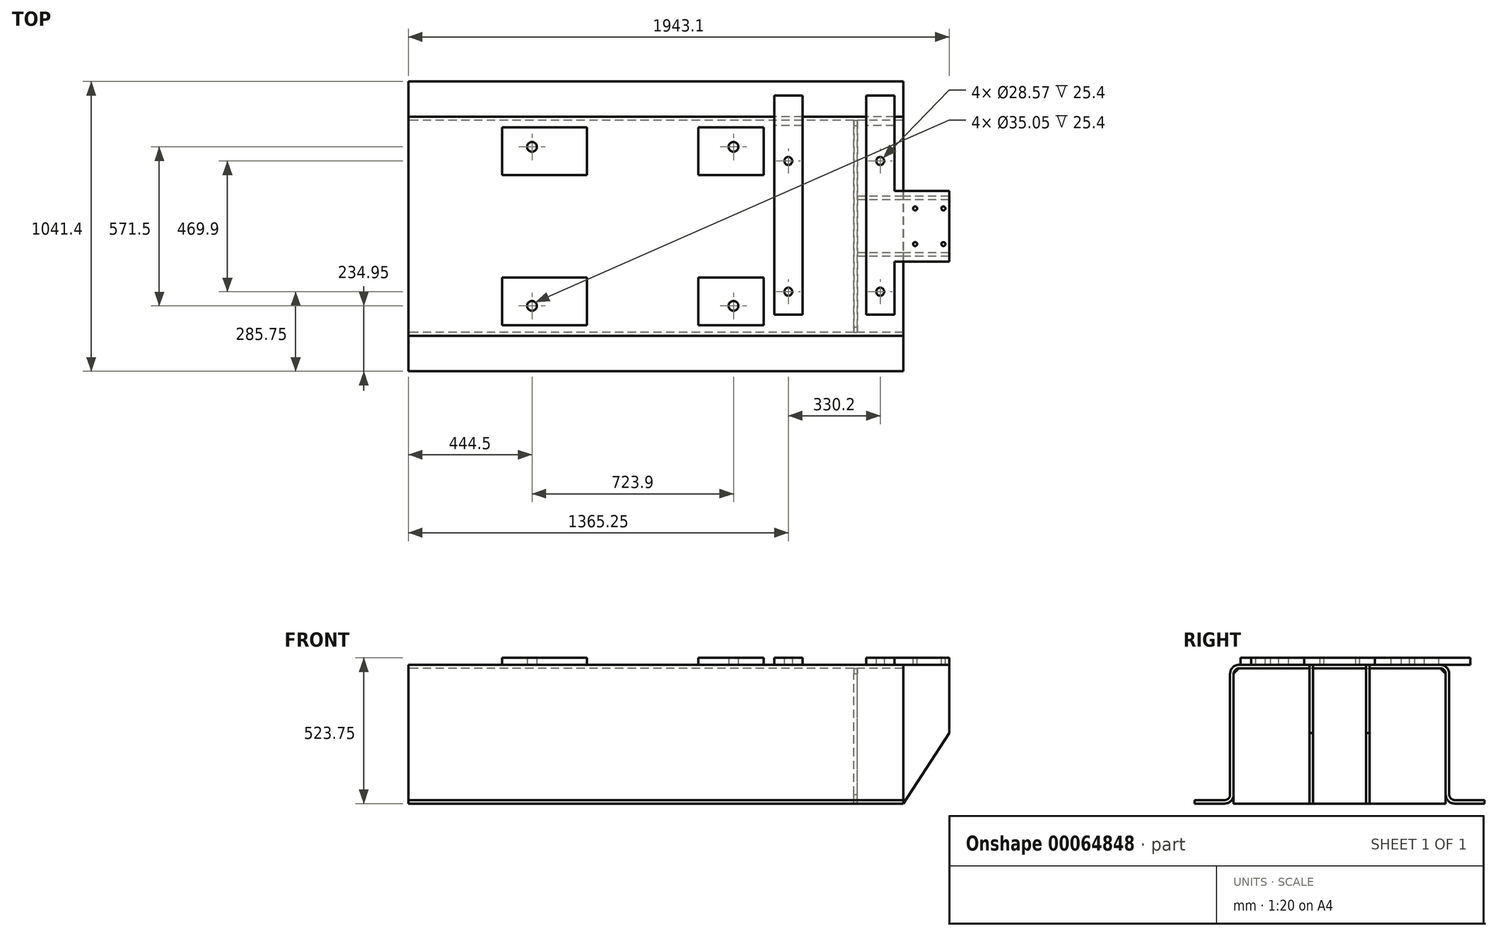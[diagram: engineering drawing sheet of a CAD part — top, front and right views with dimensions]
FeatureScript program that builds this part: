
annotation { "Feature Type Name" : "Feature", "Feature Type Description" : "" }
export const myFeature = defineFeature(function(context is Context, id is Id, definition is map)
    precondition{}
    {
        {
            var Q0;
            Q0=qCreatedBy(makeId("Right.planeOp"),FACE);
            var sketch = newSketch(context, id + "F0", { "sketchPlane" : qUnion([Q0])});
            skLineSegment(sketch, "E0", {"start": v(-520.7, 0) * mm, "end": v(-412.75, 0) * mm});
            skLineSegment(sketch, "E1.0", {"start": v(-520.7, 12.7) * mm, "end": v(-412.75, 12.7) * mm});
            skLineSegment(sketch, "E2", {"start": v(-520.7, 0) * mm, "end": v(-520.7, 12.7) * mm});
            skLineSegment(sketch, "E3", {"start": v(0, 498.35) * mm, "end": v(0, -237.5) * mm, "construction": true});
            skLineSegment(sketch, "E4.0", {"start": v(-381, 31.75) * mm, "end": v(-381, 466.6) * mm});
            skLineSegment(sketch, "E5.0", {"start": v(-393.7, 31.75) * mm, "end": v(-393.7, 466.6) * mm});
            skLineSegment(sketch, "E6.0", {"start": v(-361.95, 498.35) * mm, "end": v(0, 498.35) * mm});
            skLineSegment(sketch, "E7.0", {"start": v(-361.95, 485.65) * mm, "end": v(0, 485.65) * mm});
            skPoint(sketch, "E8.orphan", {"position": v(-520.7, 181.66) * mm});
            skPoint(sketch, "E9.visualSharp", {"position": v(-381, 485.65) * mm});
            skArc(sketch, "E9.filletArc", {"start": v(-361.95, 485.65) * mm, "mid": v(-375.42, 480.07) * mm, "end": v(-381, 466.6) * mm});
            skPoint(sketch, "E10.visualSharp", {"position": v(-393.7, 12.7) * mm});
            skArc(sketch, "E10.filletArc", {"start": v(-412.75, 12.7) * mm, "mid": v(-399.28, 18.28) * mm, "end": v(-393.7, 31.75) * mm});
            skPoint(sketch, "E11.visualSharp", {"position": v(-393.7, 498.35) * mm});
            skArc(sketch, "E11.filletArc", {"start": v(-361.95, 498.35) * mm, "mid": v(-384.4, 489.05) * mm, "end": v(-393.7, 466.6) * mm});
            skPoint(sketch, "E12.visualSharp", {"position": v(-381, 0) * mm});
            skArc(sketch, "E12.filletArc", {"start": v(-412.75, 0) * mm, "mid": v(-390.3, 9.3) * mm, "end": v(-381, 31.75) * mm});
            skLineSegment(sketch, "E13.MirrorCS", {"start": v(520.7, 0) * mm, "end": v(520.7, 12.7) * mm});
            skArc(sketch, "E14.MirrorCS", {"start": v(412.75, 12.7) * mm, "mid": v(399.28, 18.28) * mm, "end": v(393.7, 31.75) * mm});
            skArc(sketch, "E15.MirrorCS", {"start": v(412.75, 0) * mm, "mid": v(390.3, 9.3) * mm, "end": v(381, 31.75) * mm});
            skPoint(sketch, "E16.MirrorP", {"position": v(393.7, 12.7) * mm});
            skPoint(sketch, "E17.MirrorP", {"position": v(381, 0) * mm});
            skLineSegment(sketch, "E18.MirrorCS", {"start": v(520.7, 0) * mm, "end": v(412.75, 0) * mm});
            skLineSegment(sketch, "E19.MirrorCS", {"start": v(520.7, 12.7) * mm, "end": v(412.75, 12.7) * mm});
            skLineSegment(sketch, "E20.MirrorCS", {"start": v(393.7, 31.75) * mm, "end": v(393.7, 466.6) * mm});
            skLineSegment(sketch, "E21.MirrorCS", {"start": v(381, 31.75) * mm, "end": v(381, 466.6) * mm});
            skArc(sketch, "E22.MirrorCS", {"start": v(361.95, 485.65) * mm, "mid": v(375.42, 480.07) * mm, "end": v(381, 466.6) * mm});
            skArc(sketch, "E23.MirrorCS", {"start": v(361.95, 498.35) * mm, "mid": v(384.4, 489.05) * mm, "end": v(393.7, 466.6) * mm});
            skPoint(sketch, "E24.MirrorP", {"position": v(381, 485.65) * mm});
            skPoint(sketch, "E25.MirrorP", {"position": v(393.7, 498.35) * mm});
            skLineSegment(sketch, "E26.MirrorCS", {"start": v(361.95, 485.65) * mm, "end": v(0, 485.65) * mm});
            skLineSegment(sketch, "E27.MirrorCS", {"start": v(361.95, 498.35) * mm, "end": v(0, 498.35) * mm});
            skSolve(sketch);
        }
        {
            var Q0;
            Q0=qSketchRegion(id+"F0",true);
            extrude(context, id + "F1", {"entities" : qUnion([Q0]), "endBound" : BoundingType.SYMMETRIC, "depth" : 1778 * mm});
        }
        {
            var Q0;
            Q0=makeQuery(id+"F1.opExtrude","SWEPT_FACE",FACE,{"disambiguationData":[OSD([sQuery(id+"F0.wireOp",EDGE,"E6.0"),sQuery(id+"F0.wireOp",EDGE,"E27.MirrorCS")])]});
            var sketch = newSketch(context, id + "F2", { "sketchPlane" : qUnion([Q0])});
            skLineSegment(sketch, "E28.0", {"start": v(641.35, 361.95) * mm, "end": v(641.35, -361.95) * mm, "construction": true});
            skLineSegment(sketch, "E29.0", {"start": v(-82.55, 361.95) * mm, "end": v(-82.55, -361.95) * mm, "construction": true});
            skLineSegment(sketch, "E30", {"start": v(-872.47, 0) * mm, "end": v(1054.1, 0) * mm, "construction": true});
            skLineSegment(sketch, "E31.0", {"start": v(476.25, 361.95) * mm, "end": v(476.25, -361.95) * mm, "construction": true});
            skLineSegment(sketch, "E32.0", {"start": v(806.45, 361.95) * mm, "end": v(806.45, -361.95) * mm, "construction": true});
            skLineSegment(sketch, "E33.0", {"start": v(425.45, 469.9) * mm, "end": v(425.45, -317.5) * mm});
            skLineSegment(sketch, "E34.0", {"start": v(527.05, 469.9) * mm, "end": v(527.05, -317.5) * mm});
            skLineSegment(sketch, "E35.0", {"start": v(755.65, 469.9) * mm, "end": v(755.65, -317.5) * mm});
            skLineSegment(sketch, "E36.0", {"start": v(1054.1, 127) * mm, "end": v(1054.1, -127) * mm});
            skLineSegment(sketch, "E37.0", {"start": v(425.45, 469.9) * mm, "end": v(527.05, 469.9) * mm});
            skLineSegment(sketch, "E38.0", {"start": v(755.65, -317.5) * mm, "end": v(857.25, -317.5) * mm});
            skLineSegment(sketch, "E39.trimOffspring", {"start": v(755.65, 469.9) * mm, "end": v(857.25, 469.9) * mm});
            skLineSegment(sketch, "E40.trimOffspring", {"start": v(527.05, -317.5) * mm, "end": v(425.45, -317.5) * mm});
            skLineSegment(sketch, "E41.0", {"start": v(857.25, 469.9) * mm, "end": v(857.25, 127) * mm});
            skLineSegment(sketch, "E42.trimOffspring", {"start": v(857.25, -127) * mm, "end": v(1054.1, -127) * mm});
            skLineSegment(sketch, "E43.trimOffspring", {"start": v(857.25, 127) * mm, "end": v(1054.1, 127) * mm});
            skLineSegment(sketch, "E44.trimOffspring", {"start": v(857.25, -127) * mm, "end": v(857.25, -317.5) * mm});
            skLineSegment(sketch, "E45.0", {"start": v(-872.47, 234.95) * mm, "end": v(1054.1, 234.95) * mm, "construction": true});
            skCircle(sketch, "E46", {"center": v(476.25, 234.95) * mm, "radius": 14.29 * mm});
            skCircle(sketch, "E47", {"center": v(806.45, 234.95) * mm, "radius": 14.29 * mm});
            skCircle(sketch, "E48.MirrorC", {"center": v(806.45, -234.95) * mm, "radius": 14.29 * mm});
            skCircle(sketch, "E49.MirrorC", {"center": v(476.25, -234.95) * mm, "radius": 14.29 * mm});
            skSolve(sketch);
        }
        {
            var Q0;
            Q0=qSketchRegion(id+"F2",true);
            extrude(context, id + "F3", {"entities" : qUnion([Q0]), "operationType" : NewBodyOperationType.ADD, "depth" : 25.4 * mm});
        }
        {
            var Q0;
            Q0=makeQuery(id+"F3.opExtrude","CAP_FACE",FACE,{"disambiguationData":[OSD([sQuery(id+"F2.wireOp",EDGE,"E35.0"),sQuery(id+"F2.wireOp",EDGE,"E36.0"),sQuery(id+"F2.wireOp",EDGE,"E38.0"),sQuery(id+"F2.wireOp",EDGE,"E39.trimOffspring"),sQuery(id+"F2.wireOp",EDGE,"E41.0"),sQuery(id+"F2.wireOp",EDGE,"E42.trimOffspring"),sQuery(id+"F2.wireOp",EDGE,"E43.trimOffspring"),sQuery(id+"F2.wireOp",EDGE,"E44.trimOffspring"),sQuery(id+"F2.wireOp",EDGE,"E47"),sQuery(id+"F2.wireOp",EDGE,"E48.MirrorC")])],"isStart":false});
            var sketch = newSketch(context, id + "F4", { "sketchPlane" : qUnion([Q0])});
            skLineSegment(sketch, "E50", {"start": v(806.45, 234.95) * mm, "end": v(806.45, -249.24) * mm, "construction": true});
            skLineSegment(sketch, "E51", {"start": v(0, 0) * mm, "end": v(1216.03, 0) * mm, "construction": true});
            skPoint(sketch, "E51.endSnap0", {"position": v(1054.1, 0) * mm});
            skLineSegment(sketch, "E52.0", {"start": v(931.93, 234.95) * mm, "end": v(931.93, -249.24) * mm, "construction": true});
            skLineSegment(sketch, "E53.0", {"start": v(1033.53, 234.95) * mm, "end": v(1033.53, -249.24) * mm, "construction": true});
            skLineSegment(sketch, "E54.0", {"start": v(0, 64.52) * mm, "end": v(1216.03, 64.52) * mm, "construction": true});
            skLineSegment(sketch, "E55.0", {"start": v(0, -63.5) * mm, "end": v(1216.03, -63.5) * mm, "construction": true});
            skCircle(sketch, "E56", {"center": v(931.93, 64.52) * mm, "radius": 7.14 * mm});
            skCircle(sketch, "E57", {"center": v(1033.53, 64.52) * mm, "radius": 7.14 * mm});
            skCircle(sketch, "E58", {"center": v(1033.53, -63.5) * mm, "radius": 7.14 * mm});
            skCircle(sketch, "E59", {"center": v(931.93, -63.5) * mm, "radius": 7.14 * mm});
            skSolve(sketch);
        }
        {
            var Q0;
            Q0=qSketchRegion(id+"F4",true);
            extrude(context, id + "F5", {"entities" : qUnion([Q0]), "operationType" : NewBodyOperationType.REMOVE, "endBound" : BoundingType.THROUGH_ALL, "oppositeDirection" : true, "depth" : 25.4 * mm});
        }
        {
            var Q0;
            Q0=makeQuery(id+"F1.opExtrude","CAP_FACE",FACE,{"disambiguationData":[OSD([sQuery(id+"F0.wireOp",EDGE,"E0"),sQuery(id+"F0.wireOp",EDGE,"E1.0"),sQuery(id+"F0.wireOp",EDGE,"E2"),sQuery(id+"F0.wireOp",EDGE,"E4.0"),sQuery(id+"F0.wireOp",EDGE,"E5.0"),sQuery(id+"F0.wireOp",EDGE,"E6.0"),sQuery(id+"F0.wireOp",EDGE,"E7.0"),sQuery(id+"F0.wireOp",EDGE,"E9.filletArc"),sQuery(id+"F0.wireOp",EDGE,"E10.filletArc"),sQuery(id+"F0.wireOp",EDGE,"E11.filletArc"),sQuery(id+"F0.wireOp",EDGE,"E12.filletArc"),sQuery(id+"F0.wireOp",EDGE,"E13.MirrorCS"),sQuery(id+"F0.wireOp",EDGE,"E14.MirrorCS"),sQuery(id+"F0.wireOp",EDGE,"E15.MirrorCS"),sQuery(id+"F0.wireOp",EDGE,"E18.MirrorCS"),sQuery(id+"F0.wireOp",EDGE,"E19.MirrorCS"),sQuery(id+"F0.wireOp",EDGE,"E22.MirrorCS"),sQuery(id+"F0.wireOp",EDGE,"E23.MirrorCS"),sQuery(id+"F0.wireOp",EDGE,"E26.MirrorCS"),sQuery(id+"F0.wireOp",EDGE,"E27.MirrorCS"),sQuery(id+"F0.wireOp",EDGE,"E20.MirrorCS"),sQuery(id+"F0.wireOp",EDGE,"E21.MirrorCS")])],"isStart":false});
            cPlane(context, id + "F6", {"entities" : qUnion([Q0]), "cplaneType" : CPlaneType.OFFSET, "offset" : 165.1 * mm, "oppositeDirection" : true, "width" : 152.4 * mm, "height" : 152.4 * mm});
        }
        {
            var Q0;
            Q0=qCreatedBy(id+"F6.planeOp",FACE);
            var sketch = newSketch(context, id + "F7", { "sketchPlane" : qUnion([Q0])});
            skLineSegment(sketch, "E60.0", {"start": v(-361.95, 485.65) * mm, "end": v(361.95, 485.65) * mm});
            skLineSegment(sketch, "E61.0", {"start": v(-381, 0) * mm, "end": v(-381, 466.6) * mm});
            skLineSegment(sketch, "E62.0", {"start": v(381, 0) * mm, "end": v(381, 466.6) * mm});
            skLineSegment(sketch, "E63.0", {"start": v(381, 0) * mm, "end": v(-381, 0) * mm});
            skPoint(sketch, "E64.orphan", {"position": v(412.75, 0) * mm});
            skPoint(sketch, "E65.orphan", {"position": v(520.7, 0) * mm});
            skPoint(sketch, "E66.orphan", {"position": v(381, 31.75) * mm});
            skPoint(sketch, "E67.orphan", {"position": v(-381, 31.75) * mm});
            skLineSegment(sketch, "E68", {"start": v(-381, 466.6) * mm, "end": v(-361.95, 485.65) * mm});
            skLineSegment(sketch, "E69", {"start": v(361.95, 485.65) * mm, "end": v(381, 466.6) * mm});
            skSolve(sketch);
        }
        {
            var Q0;
            Q0=qSketchRegion(id+"F7",true);
            extrude(context, id + "F8", {"entities" : qUnion([Q0]), "operationType" : NewBodyOperationType.ADD, "oppositeDirection" : true, "depth" : 12.7 * mm});
        }
        {
            var Q0;
            Q0=makeQuery(id+"F8.opExtrude","CAP_FACE",FACE,{"disambiguationData":[OSD([sQuery(id+"F7.wireOp",EDGE,"E60.0"),sQuery(id+"F7.wireOp",EDGE,"E61.0"),sQuery(id+"F7.wireOp",EDGE,"E62.0"),sQuery(id+"F7.wireOp",EDGE,"E63.0"),sQuery(id+"F7.wireOp",EDGE,"E68"),sQuery(id+"F7.wireOp",EDGE,"E69")])],"isStart":true});
            var sketch = newSketch(context, id + "F9", { "sketchPlane" : qUnion([Q0])});
            skLineSegment(sketch, "E70", {"start": v(0, 0) * mm, "end": v(0, 673.02) * mm, "construction": true});
            skPoint(sketch, "E70.endSnap0", {"position": v(0, 0) * mm});
            skLineSegment(sketch, "E71.0", {"start": v(-95.25, 0) * mm, "end": v(-95.25, 673.02) * mm, "construction": true});
            skLineSegment(sketch, "E72.bottom", {"start": v(-95.25, 0) * mm, "end": v(-107.95, 0) * mm});
            skLineSegment(sketch, "E72.top", {"start": v(-95.25, 485.65) * mm, "end": v(-107.95, 485.65) * mm});
            skLineSegment(sketch, "E72.left", {"start": v(-95.25, 0) * mm, "end": v(-95.25, 485.65) * mm});
            skLineSegment(sketch, "E72.right", {"start": v(-107.95, 0) * mm, "end": v(-107.95, 485.65) * mm});
            skSolve(sketch);
        }
        {
            var Q0;
            Q0=qSketchRegion(id+"F9",true);
            var Q1;
            Q1=makeQuery(id+"F3.opExtrude","SWEPT_FACE",FACE,{"disambiguationData":[OSD([sQuery(id+"F2.wireOp",EDGE,"E36.0")])]});
            extrude(context, id + "F10", {"entities" : qUnion([Q0]), "endBound" : BoundingType.UP_TO_SURFACE, "endBoundEntityFace" : qUnion([Q1]), "depth" : 25.4 * mm});
        }
        {
            var Q0;
            Q0=makeQuery(id+"F10.opExtrude","SWEPT_FACE",FACE,{"disambiguationData":[OSD([sQuery(id+"F9.wireOp",EDGE,"E72.right")])]});
            var sketch = newSketch(context, id + "F11", { "sketchPlane" : qUnion([Q0])});
            skPoint(sketch, "E73.oppositeSnap0", {"position": v(889, 485.65) * mm});
            skLineSegment(sketch, "E73.bottom", {"start": v(1054.1, 485.65) * mm, "end": v(889, 485.65) * mm});
            skLineSegment(sketch, "E73.top", {"start": v(1054.1, 498.55) * mm, "end": v(889, 498.55) * mm});
            skLineSegment(sketch, "E73.left", {"start": v(1054.1, 485.65) * mm, "end": v(1054.1, 498.55) * mm});
            skLineSegment(sketch, "E73.right", {"start": v(889, 485.65) * mm, "end": v(889, 498.55) * mm});
            skSolve(sketch);
        }
        {
            var Q0;
            Q0=qSketchRegion(id+"F11",true);
            extrude(context, id + "F12", {"entities" : qUnion([Q0]), "oppositeDirection" : true, "depth" : 12.7 * mm});
        }
        {
            var Q0;
            Q0=makeQuery(id+"F12.opExtrude","SWEPT_BODY",BODY,{"disambiguationData":[OSD([sQuery(id+"F11.wireOp",EDGE,"E73.bottom"),sQuery(id+"F11.wireOp",EDGE,"E73.top"),sQuery(id+"F11.wireOp",EDGE,"E73.left"),sQuery(id+"F11.wireOp",EDGE,"E73.right")])]});
            var Q1;
            Q1=makeQuery(id+"F10.opExtrude","SWEPT_BODY",BODY,{"disambiguationData":[OSD([sQuery(id+"F9.wireOp",EDGE,"E72.bottom"),sQuery(id+"F9.wireOp",EDGE,"E72.top"),sQuery(id+"F9.wireOp",EDGE,"E72.left"),sQuery(id+"F9.wireOp",EDGE,"E72.right")])]});
            booleanBodies(context, id + "F13", {"operationType" : BooleanOperationType.UNION, "tools" : qUnion([Q0, Q1])});
        }
        {
            var Q0;
            Q0=makeQuery(id+"F13.opBoolean","MERGE",FACE,{"derivedFrom":[makeQuery(id+"F10.opExtrude","SWEPT_FACE",FACE,{"disambiguationData":[OSD([sQuery(id+"F9.wireOp",EDGE,"E72.right")])]}),makeQuery(id+"F12.opExtrude","CAP_FACE",FACE,{"disambiguationData":[OSD([sQuery(id+"F11.wireOp",EDGE,"E73.bottom"),sQuery(id+"F11.wireOp",EDGE,"E73.top"),sQuery(id+"F11.wireOp",EDGE,"E73.left"),sQuery(id+"F11.wireOp",EDGE,"E73.right")])],"isStart":true})]});
            var sketch = newSketch(context, id + "F14", { "sketchPlane" : qUnion([Q0])});
            skLineSegment(sketch, "E74.0", {"start": v(1054.1, 0) * mm, "end": v(723.9, 0) * mm, "construction": true});
            skLineSegment(sketch, "E75.0", {"start": v(889, 0) * mm, "end": v(889, 12.7) * mm, "construction": true});
            skLineSegment(sketch, "E76.0", {"start": v(1054.1, 254) * mm, "end": v(723.9, 254) * mm, "construction": true});
            skLineSegment(sketch, "E77", {"start": v(1054.1, 254) * mm, "end": v(889, 0) * mm});
            skLineSegment(sketch, "E78", {"start": v(889, 0) * mm, "end": v(1054.1, 0) * mm});
            skLineSegment(sketch, "E79", {"start": v(1054.1, 0) * mm, "end": v(1054.1, 254) * mm});
            skSolve(sketch);
        }
        {
            var Q0;
            Q0=qSketchRegion(id+"F14",true);
            extrude(context, id + "F15", {"entities" : qUnion([Q0]), "operationType" : NewBodyOperationType.REMOVE, "endBound" : BoundingType.THROUGH_ALL, "oppositeDirection" : true, "depth" : 25.4 * mm});
        }
        {
            var Q0;
            Q0=makeQuery(id+"F12.opExtrude","SWEPT_BODY",BODY,{"disambiguationData":[OSD([sQuery(id+"F11.wireOp",EDGE,"E73.bottom"),sQuery(id+"F11.wireOp",EDGE,"E73.top"),sQuery(id+"F11.wireOp",EDGE,"E73.left"),sQuery(id+"F11.wireOp",EDGE,"E73.right")])]});
            var Q1;
            Q1=qCreatedBy(makeId("Front.planeOp"),FACE);
            mirror(context, id + "F16", {"entities" : qUnion([Q0]), "mirrorPlane" : qUnion([Q1])});
        }
        {
            var Q0;
            {var subQ0=sQuery(id+"F0.wireOp",EDGE,"E6.0");var subQ1=sQuery(id+"F0.wireOp",EDGE,"E27.MirrorCS");var subQ9=sQuery(id+"F0.wireOp",EDGE,"E11.filletArc");Q0=makeQuery(id+"F3.boolean.opBoolean","SPLIT",FACE,{"disambiguationData":[TD([makeQuery(id+"F1.opExtrude","SWEPT_FACE",FACE,{"disambiguationData":[OSD([subQ9])]})])],"derivedFrom":makeQuery(id+"F1.opExtrude","SWEPT_FACE",FACE,{"disambiguationData":[OSD([subQ0,subQ1])]})});}
            var sketch = newSketch(context, id + "F17", { "sketchPlane" : qUnion([Q0])});
            skLineSegment(sketch, "E80", {"start": v(-968.8, 0) * mm, "end": v(1260.8, 0) * mm, "construction": true});
            skPoint(sketch, "E80.endSnap0", {"position": v(-889, 0) * mm});
            skCircle(sketch, "E81.0", {"center": v(476.25, 234.95) * mm, "radius": 14.29 * mm, "construction": true});
            skCircle(sketch, "E82.0", {"center": v(806.45, 234.95) * mm, "radius": 14.29 * mm, "construction": true});
            skLineSegment(sketch, "E83", {"start": v(476.25, 234.95) * mm, "end": v(806.45, 234.95) * mm, "construction": true});
            skLineSegment(sketch, "E84", {"start": v(641.35, 234.95) * mm, "end": v(641.35, -183.34) * mm, "construction": true});
            skLineSegment(sketch, "E85.0", {"start": v(-82.55, 234.95) * mm, "end": v(-82.55, -183.34) * mm, "construction": true});
            skLineSegment(sketch, "E86.0", {"start": v(-968.8, 184.15) * mm, "end": v(1260.8, 184.15) * mm, "construction": true});
            skLineSegment(sketch, "E87.0", {"start": v(-968.8, 355.6) * mm, "end": v(1260.8, 355.6) * mm, "construction": true});
            skLineSegment(sketch, "E88.0", {"start": v(-247.65, 234.95) * mm, "end": v(-247.65, -183.34) * mm, "construction": true});
            skLineSegment(sketch, "E89.0", {"start": v(-552.45, 355.6) * mm, "end": v(-552.45, -183.34) * mm, "construction": true});
            skLineSegment(sketch, "E90.0", {"start": v(152.4, 234.95) * mm, "end": v(152.4, -183.34) * mm, "construction": true});
            skLineSegment(sketch, "E91.0", {"start": v(387.35, 355.6) * mm, "end": v(387.35, -183.34) * mm, "construction": true});
            skLineSegment(sketch, "E92.bottom", {"start": v(-552.45, 355.6) * mm, "end": v(-247.65, 355.6) * mm});
            skLineSegment(sketch, "E92.top", {"start": v(-552.45, 184.15) * mm, "end": v(-247.65, 184.15) * mm});
            skLineSegment(sketch, "E92.left", {"start": v(-552.45, 355.6) * mm, "end": v(-552.45, 184.15) * mm});
            skLineSegment(sketch, "E92.right", {"start": v(-247.65, 355.6) * mm, "end": v(-247.65, 184.15) * mm});
            skLineSegment(sketch, "E93.bottom", {"start": v(387.35, 355.6) * mm, "end": v(152.4, 355.6) * mm});
            skLineSegment(sketch, "E93.top", {"start": v(387.35, 184.15) * mm, "end": v(152.4, 184.15) * mm});
            skLineSegment(sketch, "E93.left", {"start": v(387.35, 355.6) * mm, "end": v(387.35, 184.15) * mm});
            skLineSegment(sketch, "E93.right", {"start": v(152.4, 355.6) * mm, "end": v(152.4, 184.15) * mm});
            skLineSegment(sketch, "E94.0", {"start": v(-968.8, 285.75) * mm, "end": v(1260.8, 285.75) * mm, "construction": true});
            skLineSegment(sketch, "E95.0", {"start": v(-444.5, 285.75) * mm, "end": v(-444.5, -183.34) * mm, "construction": true});
            skLineSegment(sketch, "E96.MirrorCS", {"start": v(279.4, 285.75) * mm, "end": v(279.4, -183.34) * mm, "construction": true});
            skCircle(sketch, "E97", {"center": v(-444.5, 285.75) * mm, "radius": 17.53 * mm});
            skCircle(sketch, "E98", {"center": v(279.4, 285.75) * mm, "radius": 17.53 * mm});
            skCircle(sketch, "E99.MirrorC", {"center": v(279.4, -285.75) * mm, "radius": 17.53 * mm});
            skLineSegment(sketch, "E100.MirrorCS", {"start": v(387.35, -355.6) * mm, "end": v(387.35, -184.15) * mm});
            skLineSegment(sketch, "E101.MirrorCS", {"start": v(-552.45, -355.6) * mm, "end": v(-247.65, -355.6) * mm});
            skLineSegment(sketch, "E102.MirrorCS", {"start": v(387.35, -184.15) * mm, "end": v(152.4, -184.15) * mm});
            skLineSegment(sketch, "E103.MirrorCS", {"start": v(387.35, -355.6) * mm, "end": v(152.4, -355.6) * mm});
            skLineSegment(sketch, "E104.MirrorCS", {"start": v(-247.65, -355.6) * mm, "end": v(-247.65, -184.15) * mm});
            skLineSegment(sketch, "E105.MirrorCS", {"start": v(-552.45, -355.6) * mm, "end": v(-552.45, -184.15) * mm});
            skLineSegment(sketch, "E106.MirrorCS", {"start": v(152.4, -355.6) * mm, "end": v(152.4, -184.15) * mm});
            skLineSegment(sketch, "E107.MirrorCS", {"start": v(-552.45, -184.15) * mm, "end": v(-247.65, -184.15) * mm});
            skCircle(sketch, "E108.MirrorC", {"center": v(-444.5, -285.75) * mm, "radius": 17.53 * mm});
            skSolve(sketch);
        }
        {
            var Q0;
            Q0=qSketchRegion(id+"F17",true);
            extrude(context, id + "F18", {"entities" : qUnion([Q0]), "operationType" : NewBodyOperationType.ADD, "depth" : 25.4 * mm});
        }
    });
